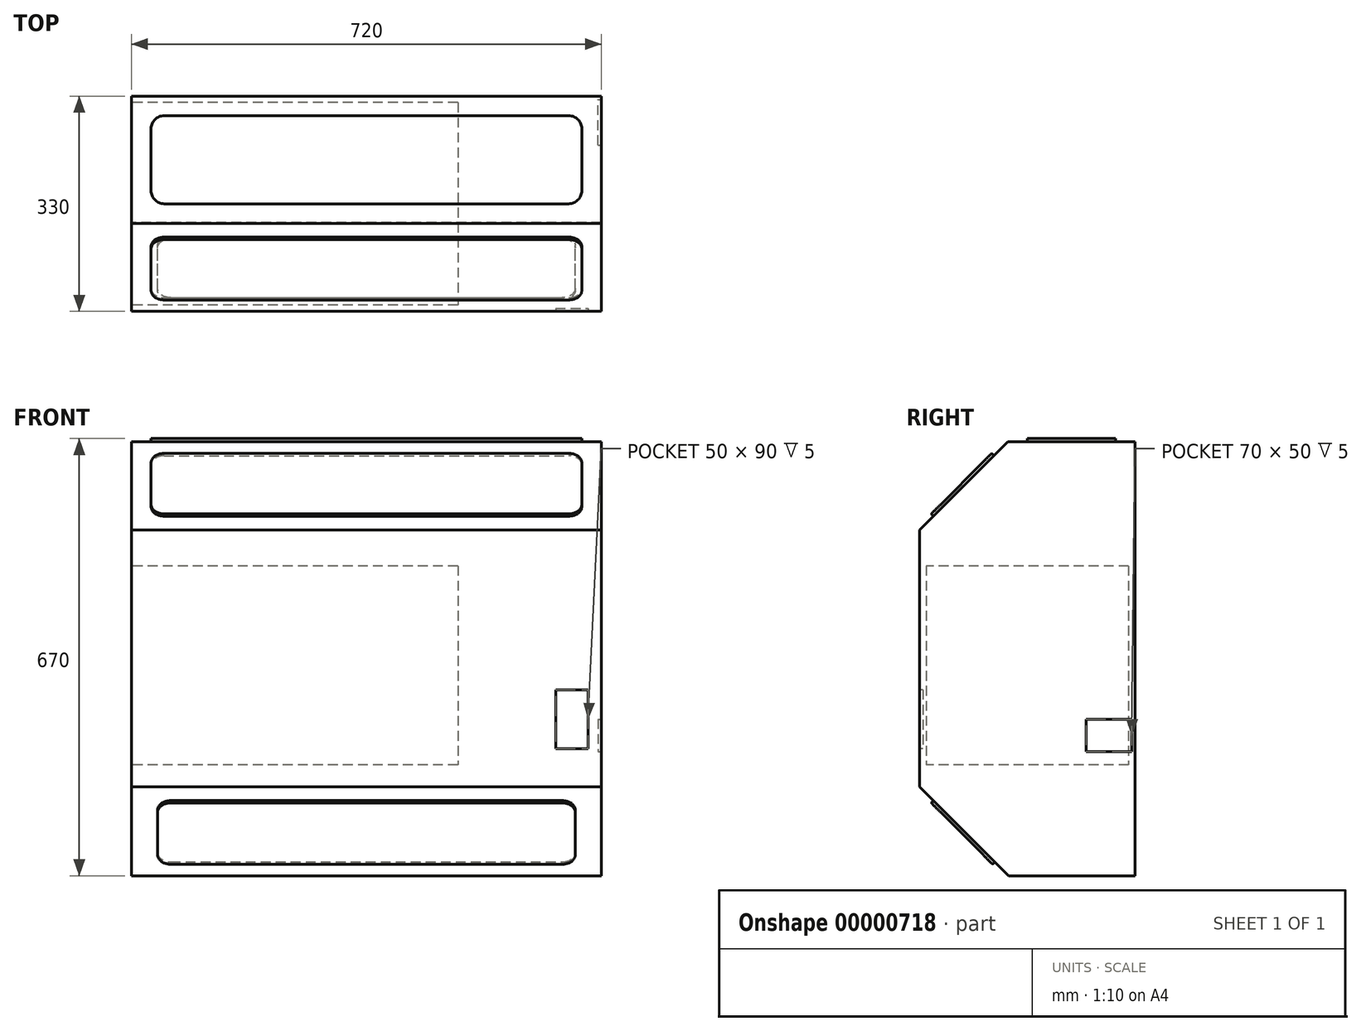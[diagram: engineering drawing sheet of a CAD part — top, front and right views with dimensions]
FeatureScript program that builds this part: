
annotation { "Feature Type Name" : "Feature", "Feature Type Description" : "" }
export const myFeature = defineFeature(function(context is Context, id is Id, definition is map)
    precondition{}
    {
        {
            var Q0;
            Q0=qCreatedBy(makeId("Right.planeOp"),FACE);
            var sketch = newSketch(context, id + "F0", { "sketchPlane" : qUnion([Q0])});
            skLineSegment(sketch, "E0.bottom", {"start": v(-30.81, 222.42) * mm, "end": v(164.19, 222.42) * mm});
            skLineSegment(sketch, "E0.top", {"start": v(-29.49, -442.58) * mm, "end": v(164.19, -442.58) * mm});
            skLineSegment(sketch, "E0.left", {"start": v(-165.81, 87.42) * mm, "end": v(-165.81, -306.25) * mm});
            skLineSegment(sketch, "E0.right", {"start": v(164.19, 222.42) * mm, "end": v(164.19, -442.58) * mm});
            skLineSegment(sketch, "E1", {"start": v(-29.49, -442.58) * mm, "end": v(-165.81, -306.25) * mm});
            skLineSegment(sketch, "E2", {"start": v(-165.81, 87.42) * mm, "end": v(-30.81, 222.42) * mm});
            skSolve(sketch);
        }
        {
            var Q0;
            Q0=makeQuery(id+"F0.imprint","IMPRINT",FACE,{"disambiguationData":[TD([[makeQuery(id+"F0.imprint","IMPRINT",EDGE,{"derivedFrom":sQuery(id+"F0.wireOp",EDGE,"E0.bottom")}),-1.0]])]});
            extrude(context, id + "F1", {"entities" : qUnion([Q0]), "depth" : 720 * mm});
        }
        {
            var Q0;
            Q0=makeQuery(id+"F1.opExtrude","SWEPT_FACE",FACE,{"disambiguationData":[OSD([sQuery(id+"F0.wireOp",EDGE,"E1")])]});
            var sketch = newSketch(context, id + "F2", { "sketchPlane" : qUnion([Q0])});
            skLineSegment(sketch, "E3.bottom", {"start": v(60, -129.3) * mm, "end": v(660, -129.3) * mm});
            skLineSegment(sketch, "E3.top", {"start": v(60, -262.1) * mm, "end": v(660, -262.1) * mm});
            skLineSegment(sketch, "E3.left", {"start": v(40, -149.3) * mm, "end": v(40, -242.1) * mm});
            skLineSegment(sketch, "E3.right", {"start": v(680, -149.3) * mm, "end": v(680, -242.1) * mm});
            skPoint(sketch, "E4.visualSharp", {"position": v(40, -129.3) * mm});
            skArc(sketch, "E4.filletArc", {"start": v(60, -129.3) * mm, "mid": v(45.86, -135.17) * mm, "end": v(40, -149.3) * mm});
            skPoint(sketch, "E5.visualSharp", {"position": v(40, -262.1) * mm});
            skArc(sketch, "E5.filletArc", {"start": v(40, -242.1) * mm, "mid": v(45.86, -256.24) * mm, "end": v(60, -262.1) * mm});
            skPoint(sketch, "E6.visualSharp", {"position": v(680, -262.1) * mm});
            skArc(sketch, "E6.filletArc", {"start": v(660, -262.1) * mm, "mid": v(674.14, -256.24) * mm, "end": v(680, -242.1) * mm});
            skPoint(sketch, "E7.visualSharp", {"position": v(680, -129.3) * mm});
            skArc(sketch, "E7.filletArc", {"start": v(680, -149.3) * mm, "mid": v(674.14, -135.17) * mm, "end": v(660, -129.3) * mm});
            skSolve(sketch);
        }
        {
            var Q0;
            Q0=makeQuery(id+"F2.imprint","IMPRINT",FACE,{"disambiguationData":[TD([[makeQuery(id+"F2.imprint","IMPRINT",EDGE,{"derivedFrom":sQuery(id+"F2.wireOp",EDGE,"E3.bottom")}),-1.0]])]});
            extrude(context, id + "F3", {"entities" : qUnion([Q0]), "operationType" : NewBodyOperationType.ADD, "depth" : 5 * mm});
        }
        {
            var Q0;
            Q0=makeQuery(id+"F1.opExtrude","SWEPT_FACE",FACE,{"disambiguationData":[OSD([sQuery(id+"F0.wireOp",EDGE,"E0.bottom")])]});
            var sketch = newSketch(context, id + "F4", { "sketchPlane" : qUnion([Q0])});
            skLineSegment(sketch, "E8.bottom", {"start": v(50, 134.19) * mm, "end": v(670, 134.19) * mm});
            skLineSegment(sketch, "E8.top", {"start": v(50, -0.81) * mm, "end": v(670, -0.81) * mm});
            skLineSegment(sketch, "E8.left", {"start": v(30, 114.19) * mm, "end": v(30, 19.19) * mm});
            skLineSegment(sketch, "E8.right", {"start": v(690, 114.19) * mm, "end": v(690, 19.19) * mm});
            skPoint(sketch, "E9.visualSharp", {"position": v(30, 134.19) * mm});
            skArc(sketch, "E9.filletArc", {"start": v(50, 134.19) * mm, "mid": v(35.86, 128.33) * mm, "end": v(30, 114.19) * mm});
            skPoint(sketch, "E10.visualSharp", {"position": v(30, -0.81) * mm});
            skArc(sketch, "E10.filletArc", {"start": v(30, 19.19) * mm, "mid": v(35.86, 5.05) * mm, "end": v(50, -0.81) * mm});
            skPoint(sketch, "E11.visualSharp", {"position": v(690, -0.81) * mm});
            skArc(sketch, "E11.filletArc", {"start": v(670, -0.81) * mm, "mid": v(684.14, 5.05) * mm, "end": v(690, 19.19) * mm});
            skPoint(sketch, "E12.visualSharp", {"position": v(690, 134.19) * mm});
            skArc(sketch, "E12.filletArc", {"start": v(690, 114.19) * mm, "mid": v(684.14, 128.33) * mm, "end": v(670, 134.19) * mm});
            skSolve(sketch);
        }
        {
            var Q0;
            Q0=makeQuery(id+"F4.imprint","IMPRINT",FACE,{"disambiguationData":[TD([[makeQuery(id+"F4.imprint","IMPRINT",EDGE,{"derivedFrom":sQuery(id+"F4.wireOp",EDGE,"E8.bottom")}),-1.0]])]});
            extrude(context, id + "F5", {"entities" : qUnion([Q0]), "operationType" : NewBodyOperationType.ADD, "depth" : 5 * mm});
        }
        {
            var Q0;
            Q0=makeQuery(id+"F1.opExtrude","SWEPT_FACE",FACE,{"disambiguationData":[OSD([sQuery(id+"F0.wireOp",EDGE,"E2")])]});
            var sketch = newSketch(context, id + "F6", { "sketchPlane" : qUnion([Q0])});
            skLineSegment(sketch, "E13.bottom", {"start": v(50, 105.5) * mm, "end": v(670, 105.5) * mm});
            skLineSegment(sketch, "E13.top", {"start": v(50, -25.43) * mm, "end": v(670, -25.43) * mm});
            skLineSegment(sketch, "E13.left", {"start": v(30, 85.5) * mm, "end": v(30, -5.43) * mm});
            skLineSegment(sketch, "E13.right", {"start": v(690, 85.5) * mm, "end": v(690, -5.43) * mm});
            skPoint(sketch, "E14.visualSharp", {"position": v(30, 105.5) * mm});
            skArc(sketch, "E14.filletArc", {"start": v(50, 105.5) * mm, "mid": v(35.86, 99.63) * mm, "end": v(30, 85.5) * mm});
            skPoint(sketch, "E15.visualSharp", {"position": v(30, -25.43) * mm});
            skArc(sketch, "E15.filletArc", {"start": v(30, -5.43) * mm, "mid": v(35.86, -19.57) * mm, "end": v(50, -25.43) * mm});
            skPoint(sketch, "E16.visualSharp", {"position": v(690, -25.43) * mm});
            skArc(sketch, "E16.filletArc", {"start": v(670, -25.43) * mm, "mid": v(684.14, -19.57) * mm, "end": v(690, -5.43) * mm});
            skPoint(sketch, "E17.visualSharp", {"position": v(690, 105.5) * mm});
            skArc(sketch, "E17.filletArc", {"start": v(690, 85.5) * mm, "mid": v(684.14, 99.63) * mm, "end": v(670, 105.5) * mm});
            skSolve(sketch);
        }
        {
            var Q0;
            Q0=makeQuery(id+"F6.imprint","IMPRINT",FACE,{"disambiguationData":[TD([[makeQuery(id+"F6.imprint","IMPRINT",EDGE,{"derivedFrom":sQuery(id+"F6.wireOp",EDGE,"E13.bottom")}),-1.0]])]});
            extrude(context, id + "F7", {"entities" : qUnion([Q0]), "operationType" : NewBodyOperationType.ADD, "depth" : 5 * mm});
        }
        {
            var Q0;
            Q0=makeQuery(id+"F1.opExtrude","CAP_FACE",FACE,{"disambiguationData":[OSD([sQuery(id+"F0.wireOp",EDGE,"E0.bottom"),sQuery(id+"F0.wireOp",EDGE,"E0.top"),sQuery(id+"F0.wireOp",EDGE,"E0.left"),sQuery(id+"F0.wireOp",EDGE,"E0.right"),sQuery(id+"F0.wireOp",EDGE,"E1"),sQuery(id+"F0.wireOp",EDGE,"E2")])],"isStart":true});
            var sketch = newSketch(context, id + "F8", { "sketchPlane" : qUnion([Q0])});
            skLineSegment(sketch, "E18.bottom", {"start": v(-154.19, 32.42) * mm, "end": v(155.81, 32.42) * mm});
            skLineSegment(sketch, "E18.top", {"start": v(-154.19, -272.58) * mm, "end": v(155.81, -272.58) * mm});
            skLineSegment(sketch, "E18.left", {"start": v(-154.19, 32.42) * mm, "end": v(-154.19, -272.58) * mm});
            skLineSegment(sketch, "E18.right", {"start": v(155.81, 32.42) * mm, "end": v(155.81, -272.58) * mm});
            skSolve(sketch);
        }
        {
            var Q0;
            Q0=makeQuery(id+"F8.imprint","IMPRINT",FACE,{"disambiguationData":[TD([[makeQuery(id+"F8.imprint","IMPRINT",EDGE,{"derivedFrom":sQuery(id+"F8.wireOp",EDGE,"E18.bottom")}),-1.0]])]});
            extrude(context, id + "F9", {"entities" : qUnion([Q0]), "operationType" : NewBodyOperationType.REMOVE, "oppositeDirection" : true, "depth" : 500 * mm});
        }
        {
            var Q0;
            Q0=makeQuery(id+"F1.opExtrude","SWEPT_FACE",FACE,{"disambiguationData":[OSD([sQuery(id+"F0.wireOp",EDGE,"E0.left")])]});
            var sketch = newSketch(context, id + "F10", { "sketchPlane" : qUnion([Q0])});
            skLineSegment(sketch, "E19.bottom", {"start": v(650, -157.58) * mm, "end": v(700, -157.58) * mm});
            skLineSegment(sketch, "E19.top", {"start": v(650, -247.58) * mm, "end": v(700, -247.58) * mm});
            skLineSegment(sketch, "E19.left", {"start": v(650, -157.58) * mm, "end": v(650, -247.58) * mm});
            skLineSegment(sketch, "E19.right", {"start": v(700, -157.58) * mm, "end": v(700, -247.58) * mm});
            skSolve(sketch);
        }
        {
            var Q0;
            Q0=makeQuery(id+"F10.imprint","IMPRINT",FACE,{"disambiguationData":[TD([[makeQuery(id+"F10.imprint","IMPRINT",EDGE,{"derivedFrom":sQuery(id+"F10.wireOp",EDGE,"E19.bottom")}),-1.0]])]});
            extrude(context, id + "F11", {"entities" : qUnion([Q0]), "operationType" : NewBodyOperationType.REMOVE, "oppositeDirection" : true, "depth" : 5 * mm});
        }
        {
            var Q0;
            Q0=makeQuery(id+"F1.opExtrude","CAP_FACE",FACE,{"disambiguationData":[OSD([sQuery(id+"F0.wireOp",EDGE,"E0.bottom"),sQuery(id+"F0.wireOp",EDGE,"E0.top"),sQuery(id+"F0.wireOp",EDGE,"E0.left"),sQuery(id+"F0.wireOp",EDGE,"E0.right"),sQuery(id+"F0.wireOp",EDGE,"E1"),sQuery(id+"F0.wireOp",EDGE,"E2")])],"isStart":false});
            var sketch = newSketch(context, id + "F12", { "sketchPlane" : qUnion([Q0])});
            skLineSegment(sketch, "E20.bottom", {"start": v(89.19, -202.58) * mm, "end": v(159.19, -202.58) * mm});
            skLineSegment(sketch, "E20.top", {"start": v(89.19, -252.58) * mm, "end": v(159.19, -252.58) * mm});
            skLineSegment(sketch, "E20.left", {"start": v(89.19, -202.58) * mm, "end": v(89.19, -252.58) * mm});
            skLineSegment(sketch, "E20.right", {"start": v(159.19, -202.58) * mm, "end": v(159.19, -252.58) * mm});
            skSolve(sketch);
        }
        {
            var Q0;
            Q0=makeQuery(id+"F12.imprint","IMPRINT",FACE,{"disambiguationData":[TD([[makeQuery(id+"F12.imprint","IMPRINT",EDGE,{"derivedFrom":sQuery(id+"F12.wireOp",EDGE,"E20.bottom")}),-1.0]])]});
            extrude(context, id + "F13", {"entities" : qUnion([Q0]), "operationType" : NewBodyOperationType.REMOVE, "oppositeDirection" : true, "depth" : 5 * mm});
        }
    });
